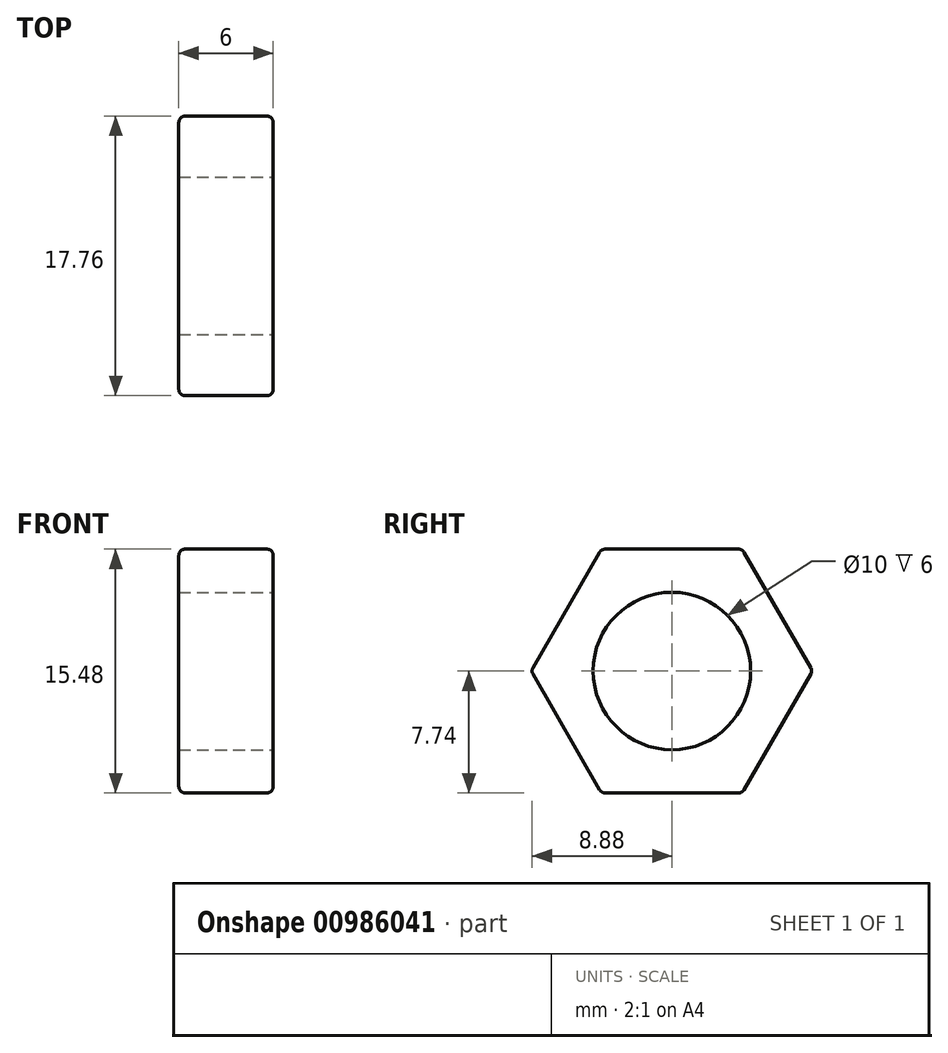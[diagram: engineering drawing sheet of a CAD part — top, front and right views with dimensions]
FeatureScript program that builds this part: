
annotation { "Feature Type Name" : "Feature", "Feature Type Description" : "" }
export const myFeature = defineFeature(function(context is Context, id is Id, definition is map)
    precondition{}
    {
        {
            var Q0;
            Q0=qCreatedBy(makeId("Right.planeOp"),FACE);
            var sketch = newSketch(context, id + "F0", { "sketchPlane" : qUnion([Q0])});
            skLineSegment(sketch, "E0", {"start": v(-4.47, 7.74) * mm, "end": v(4.47, 7.74) * mm});
            skLineSegment(sketch, "E1", {"start": v(4.47, 7.74) * mm, "end": v(8.94, 0) * mm});
            skLineSegment(sketch, "E2", {"start": v(4.47, -7.74) * mm, "end": v(8.94, 0) * mm});
            skLineSegment(sketch, "E3", {"start": v(4.47, -7.74) * mm, "end": v(-4.47, -7.74) * mm});
            skLineSegment(sketch, "E4", {"start": v(-8.94, 0) * mm, "end": v(-4.47, -7.74) * mm});
            skLineSegment(sketch, "E5", {"start": v(-8.94, 0) * mm, "end": v(-4.47, 7.74) * mm});
            skPoint(sketch, "E6.MirrorCS.start.orphan", {"position": v(0, 0) * mm});
            skCircle(sketch, "E7", {"center": v(0, 0) * mm, "radius": 5 * mm});
            skSolve(sketch);
        }
        {
            var Q0;
            Q0=makeQuery(id+"F0.imprint","IMPRINT",FACE,{"disambiguationData":[TD([[makeQuery(id+"F0.imprint","IMPRINT",EDGE,{"derivedFrom":sQuery(id+"F0.wireOp",EDGE,"E0")}),-1.0]])]});
            extrude(context, id + "F1", {"entities" : qUnion([Q0]), "oppositeDirection" : true, "depth" : 6 * mm, "offsetDistance" : 25 * mm});
        }
        {
            var Q0;
            Q0=makeQuery(id+"F1.opExtrude","SWEPT_EDGE",EDGE,{"disambiguationData":[OSD([sQuery(id+"F0.wireOp",EDGE,"E0"),sQuery(id+"F0.wireOp",EDGE,"E1")])]});
            var Q1;
            Q1=makeQuery(id+"F1.opExtrude","SWEPT_EDGE",EDGE,{"disambiguationData":[OSD([sQuery(id+"F0.wireOp",EDGE,"E1"),sQuery(id+"F0.wireOp",EDGE,"E2")])]});
            var Q2;
            Q2=makeQuery(id+"F1.opExtrude","SWEPT_EDGE",EDGE,{"disambiguationData":[OSD([sQuery(id+"F0.wireOp",EDGE,"E2"),sQuery(id+"F0.wireOp",EDGE,"E3")])]});
            var Q3;
            Q3=makeQuery(id+"F1.opExtrude","SWEPT_EDGE",EDGE,{"disambiguationData":[OSD([sQuery(id+"F0.wireOp",EDGE,"E3"),sQuery(id+"F0.wireOp",EDGE,"E4")])]});
            var Q4;
            Q4=makeQuery(id+"F1.opExtrude","SWEPT_EDGE",EDGE,{"disambiguationData":[OSD([sQuery(id+"F0.wireOp",EDGE,"E4"),sQuery(id+"F0.wireOp",EDGE,"E5")])]});
            var Q5;
            Q5=makeQuery(id+"F1.opExtrude","CAP_EDGE",EDGE,{"disambiguationData":[OSD([sQuery(id+"F0.wireOp",EDGE,"E4")])],"isStart":true});
            var Q6;
            Q6=makeQuery(id+"F1.opExtrude","CAP_EDGE",EDGE,{"disambiguationData":[OSD([sQuery(id+"F0.wireOp",EDGE,"E3")])],"isStart":true});
            var Q7;
            Q7=makeQuery(id+"F1.opExtrude","CAP_EDGE",EDGE,{"disambiguationData":[OSD([sQuery(id+"F0.wireOp",EDGE,"E2")])],"isStart":true});
            var Q8;
            Q8=makeQuery(id+"F1.opExtrude","SWEPT_FACE",FACE,{"disambiguationData":[OSD([sQuery(id+"F0.wireOp",EDGE,"E1")])]});
            var Q9;
            Q9=makeQuery(id+"F1.opExtrude","SWEPT_FACE",FACE,{"disambiguationData":[OSD([sQuery(id+"F0.wireOp",EDGE,"E2")])]});
            var Q10;
            Q10=makeQuery(id+"F1.opExtrude","SWEPT_FACE",FACE,{"disambiguationData":[OSD([sQuery(id+"F0.wireOp",EDGE,"E3")])]});
            var Q11;
            Q11=makeQuery(id+"F1.opExtrude","SWEPT_FACE",FACE,{"disambiguationData":[OSD([sQuery(id+"F0.wireOp",EDGE,"E4")])]});
            var Q12;
            Q12=makeQuery(id+"F1.opExtrude","SWEPT_FACE",FACE,{"disambiguationData":[OSD([sQuery(id+"F0.wireOp",EDGE,"E5")])]});
            var Q13;
            Q13=makeQuery(id+"F1.opExtrude","SWEPT_FACE",FACE,{"disambiguationData":[OSD([sQuery(id+"F0.wireOp",EDGE,"E0")])]});
            fillet(context, id + "F2", {"entities" : qUnion([Q0, Q1, Q2, Q3, Q4, Q5, Q6, Q7, Q8, Q9, Q10, Q11, Q12, Q13]), "radius" : 0.4 * mm, "tangentPropagation" : true, "allowEdgeOverflow" : false});
        }
    });
